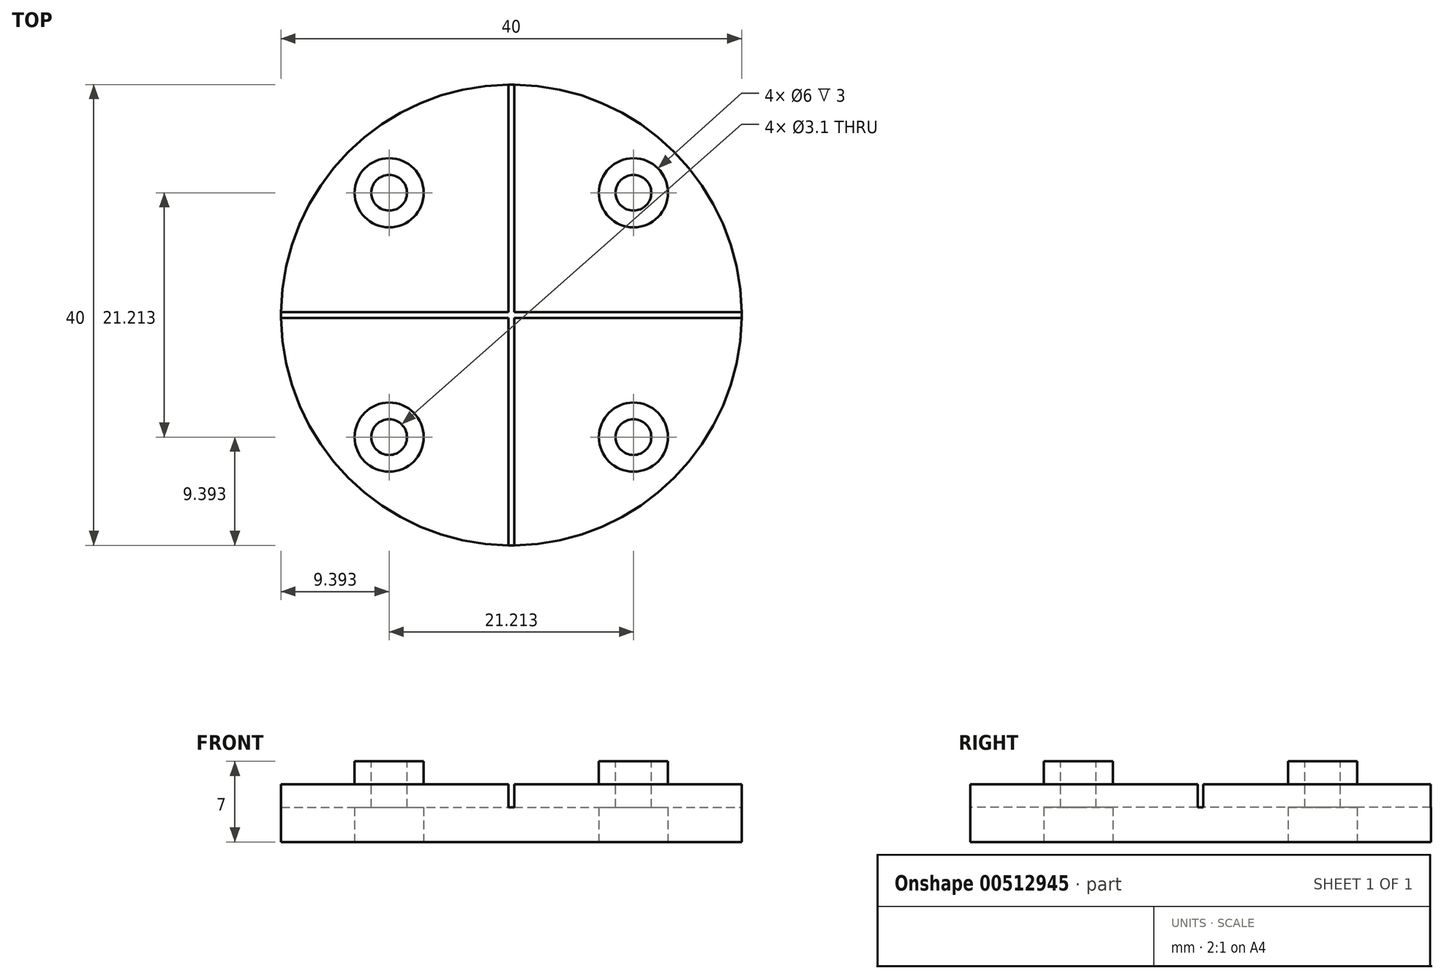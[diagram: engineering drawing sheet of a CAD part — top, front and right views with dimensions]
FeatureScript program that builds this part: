
annotation { "Feature Type Name" : "Feature", "Feature Type Description" : "" }
export const myFeature = defineFeature(function(context is Context, id is Id, definition is map)
    precondition{}
    {
        {
            var Q0;
            Q0=qCreatedBy(makeId("Top.planeOp"),FACE);
            var sketch = newSketch(context, id + "F0", { "sketchPlane" : qUnion([Q0])});
            skCircle(sketch, "E0", {"center": v(0, 0) * mm, "radius": 20 * mm});
            skSolve(sketch);
        }
        {
            var Q0;
            Q0 = qSketchRegion(id + "F0", true);
            extrude(context, id + "F1", {"entities" : qUnion([Q0]), "depth" : 5 * mm});
        }
        {
            var Q0;
            Q0=makeQuery(id+"F1.opExtrude","CAP_FACE",FACE,{"disambiguationData":[OSD([sQuery(id+"F0.wireOp",EDGE,"E0")])],"isStart":false});
            var sketch = newSketch(context, id + "F2", { "sketchPlane" : qUnion([Q0])});
            skLineSegment(sketch, "E1.bottom", {"start": v(-0.25, 21.28) * mm, "end": v(0.25, 21.28) * mm});
            skLineSegment(sketch, "E1.top", {"start": v(-0.25, -22.1) * mm, "end": v(0.25, -22.1) * mm});
            skLineSegment(sketch, "E1.left", {"start": v(-0.25, 21.28) * mm, "end": v(-0.25, -22.1) * mm});
            skLineSegment(sketch, "E1.right", {"start": v(0.25, 21.28) * mm, "end": v(0.25, -22.1) * mm});
            skLineSegment(sketch, "E2", {"start": v(0, 20) * mm, "end": v(0, -20.96) * mm, "construction": true});
            skLineSegment(sketch, "E3", {"start": v(-21.2, 0) * mm, "end": v(24.9, 0) * mm, "construction": true});
            skLineSegment(sketch, "E4.bottom", {"start": v(-22.12, 0.25) * mm, "end": v(23.6, 0.25) * mm});
            skLineSegment(sketch, "E4.top", {"start": v(-22.12, -0.25) * mm, "end": v(23.6, -0.25) * mm});
            skLineSegment(sketch, "E4.left", {"start": v(-22.12, 0.25) * mm, "end": v(-22.12, -0.25) * mm});
            skLineSegment(sketch, "E4.right", {"start": v(23.6, 0.25) * mm, "end": v(23.6, -0.25) * mm});
            skSolve(sketch);
        }
        {
            var Q0;
            Q0 = qSketchRegion(id + "F2", true);
            extrude(context, id + "F3", {"entities" : qUnion([Q0]), "operationType" : NewBodyOperationType.REMOVE, "oppositeDirection" : true, "depth" : 2 * mm});
        }
        {
            var Q0;
            {var subQ0=sQuery(id+"F0.wireOp",EDGE,"E0");var subQ1=sQuery(id+"F2.wireOp",EDGE,"E4.bottom");var subQ2=sQuery(id+"F2.wireOp",EDGE,"E1.left");var subQ3=makeQuery(id+"F2.imprint","INTERSECT",VERTEX,{"derivedFrom":[subQ2,subQ1]});var subQ7=makeQuery(id+"F1.opExtrude","CAP_EDGE",EDGE,{"disambiguationData":[OSD([subQ0])],"isStart":false});var subQ10=makeQuery(id+"F2.imprint","INTERSECT",VERTEX,{"disambiguationData":[OD(0.0)],"derivedFrom":[subQ7,subQ2]});Q0=makeQuery(id+"F3.boolean.opBoolean","SPLIT",FACE,{"disambiguationData":[TD([makeQuery(id+"F3.opExtrude","SWEPT_FACE",FACE,{"disambiguationData":[OSD([subQ2]),TDD([makeQuery(id+"F2.imprint","IMPRINT",EDGE,{"disambiguationData":[TD([[makeQuery(id+"F2.imprint","INTERSECT",VERTEX,{"derivedFrom":[sQuery(id+"F2.wireOp",EDGE,"E1.bottom"),subQ2]}),-1.0]])],"derivedFrom":subQ2}),makeQuery(id+"F2.imprint","IMPRINT",EDGE,{"disambiguationData":[TD([[subQ10,-1.0]])],"derivedFrom":subQ2}),makeQuery(id+"F2.imprint","IMPRINT",EDGE,{"disambiguationData":[TD([[subQ3,1.0]])],"derivedFrom":subQ2})])]})])],"derivedFrom":makeQuery(id+"F1.opExtrude","CAP_FACE",FACE,{"disambiguationData":[OSD([subQ0])],"isStart":false})});}
            var sketch = newSketch(context, id + "F4", { "sketchPlane" : qUnion([Q0])});
            skLineSegment(sketch, "E5", {"start": v(-21.04, 21.04) * mm, "end": v(0, 0) * mm, "construction": true});
            skLineSegment(sketch, "E6", {"start": v(0, 0) * mm, "end": v(20.97, -20.97) * mm, "construction": true});
            skLineSegment(sketch, "E7", {"start": v(0, 0) * mm, "end": v(21.21, 21.21) * mm, "construction": true});
            skLineSegment(sketch, "E8", {"start": v(0, 0) * mm, "end": v(-21.21, -21.21) * mm, "construction": true});
            skCircle(sketch, "E9", {"center": v(10.6, -10.6) * mm, "radius": 1.55 * mm});
            skCircle(sketch, "E10", {"center": v(10.6, 10.6) * mm, "radius": 1.55 * mm});
            skCircle(sketch, "E11", {"center": v(-10.6, 10.6) * mm, "radius": 1.55 * mm});
            skCircle(sketch, "E12", {"center": v(-10.6, -10.6) * mm, "radius": 1.55 * mm});
            skSolve(sketch);
        }
        {
            var Q0;
            Q0=makeQuery(id+"F1.opExtrude","CAP_FACE",FACE,{"disambiguationData":[OSD([sQuery(id+"F0.wireOp",EDGE,"E0")])],"isStart":true});
            var sketch = newSketch(context, id + "F5", { "sketchPlane" : qUnion([Q0])});
            skCircle(sketch, "E13", {"center": v(-10.6, 10.6) * mm, "radius": 3 * mm});
            skCircle(sketch, "E14", {"center": v(10.6, 10.6) * mm, "radius": 3 * mm});
            skCircle(sketch, "E15", {"center": v(10.6, -10.6) * mm, "radius": 3 * mm});
            skCircle(sketch, "E16", {"center": v(-10.6, -10.6) * mm, "radius": 3 * mm});
            skSolve(sketch);
        }
        {
            var Q0;
            Q0 = qSketchRegion(id + "F5", true);
            extrude(context, id + "F6", {"entities" : qUnion([Q0]), "operationType" : NewBodyOperationType.ADD, "oppositeDirection" : true, "depth" : 7 * mm, "offsetDistance" : 25 * mm});
        }
        {
            var Q0;
            Q0 = qSketchRegion(id + "F5", true);
            extrude(context, id + "F7", {"entities" : qUnion([Q0]), "operationType" : NewBodyOperationType.REMOVE, "oppositeDirection" : true, "depth" : 3 * mm});
        }
        {
            var Q0;
            Q0 = qSketchRegion(id + "F4", true);
            extrude(context, id + "F8", {"entities" : qUnion([Q0]), "operationType" : NewBodyOperationType.REMOVE, "endBound" : BoundingType.THROUGH_ALL, "oppositeDirection" : true, "depth" : 25 * mm, "offsetDistance" : 25 * mm});
        }
        {
            var Q0;
            Q0 = qSketchRegion(id + "F4", true);
            extrude(context, id + "F9", {"entities" : qUnion([Q0]), "operationType" : NewBodyOperationType.REMOVE, "endBound" : BoundingType.THROUGH_ALL, "depth" : 25 * mm, "offsetDistance" : 25 * mm});
        }
    });
